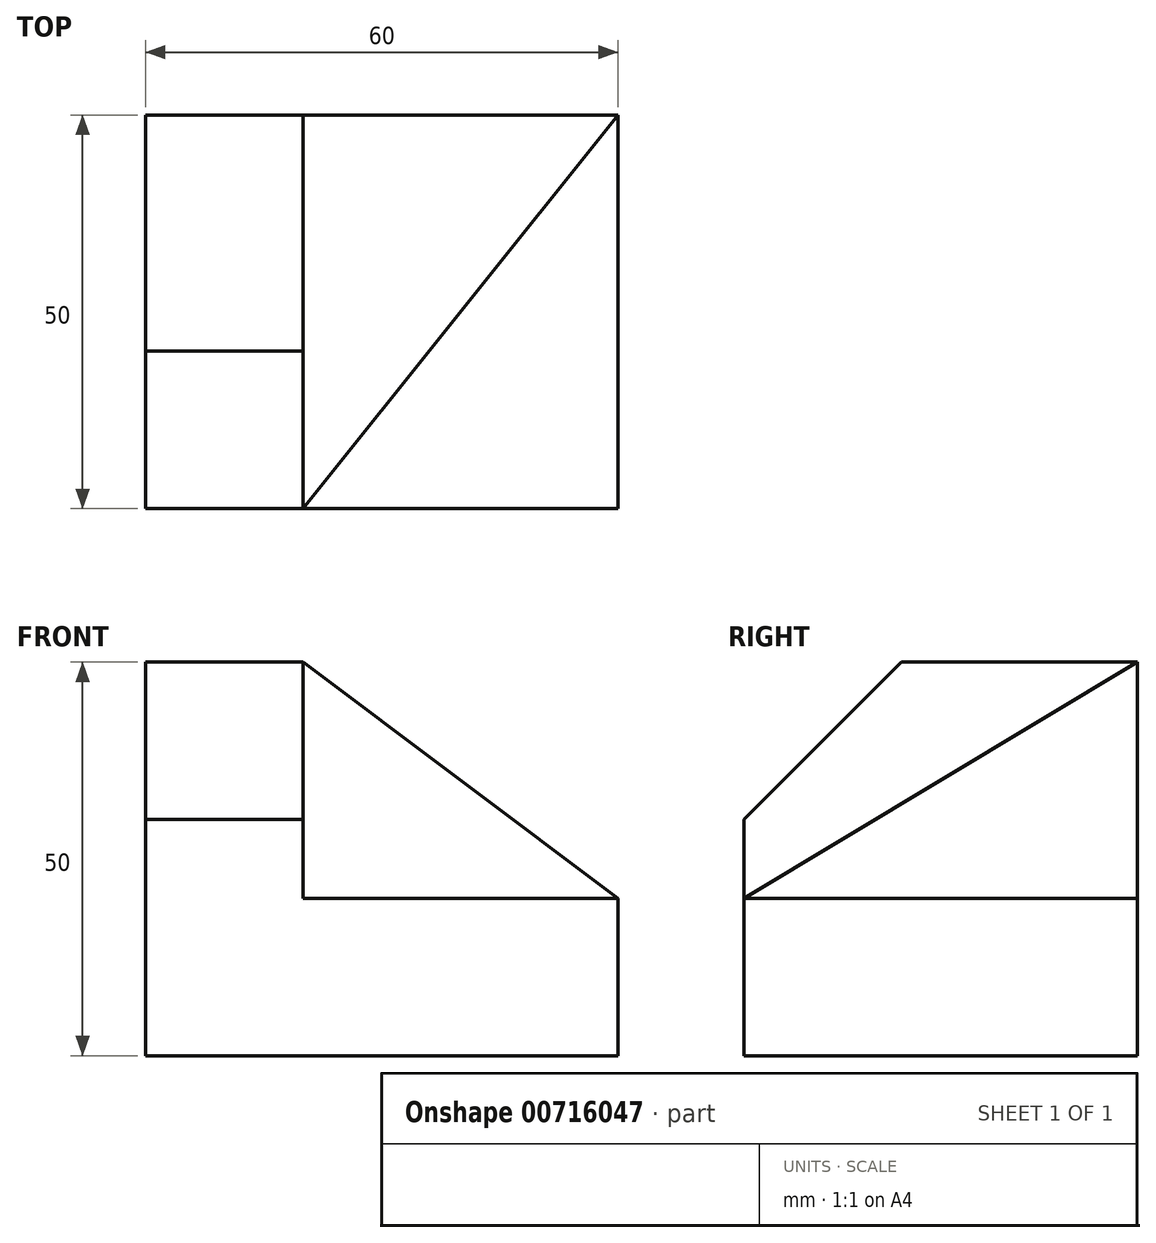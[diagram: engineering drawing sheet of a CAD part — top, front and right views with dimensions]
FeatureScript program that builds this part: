
annotation { "Feature Type Name" : "Feature", "Feature Type Description" : "" }
export const myFeature = defineFeature(function(context is Context, id is Id, definition is map)
    precondition{}
    {
        {
            var Q0;
            Q0=qCreatedBy(makeId("Top.planeOp"),FACE);
            var sketch = newSketch(context, id + "F0", { "sketchPlane" : qUnion([Q0])});
            skLineSegment(sketch, "E0.bottom", {"start": v(0, 0) * mm, "end": v(60, 0) * mm});
            skLineSegment(sketch, "E0.top", {"start": v(0, 50) * mm, "end": v(60, 50) * mm});
            skLineSegment(sketch, "E0.left", {"start": v(0, 0) * mm, "end": v(0, 50) * mm});
            skLineSegment(sketch, "E0.right", {"start": v(60, 0) * mm, "end": v(60, 50) * mm});
            skSolve(sketch);
        }
        {
            var Q0;
            Q0=makeQuery(id+"F0.imprint","IMPRINT",FACE,{"disambiguationData":[TD([[makeQuery(id+"F0.imprint","IMPRINT",EDGE,{"derivedFrom":sQuery(id+"F0.wireOp",EDGE,"E0.bottom")}),1.0]])]});
            extrude(context, id + "F1", {"entities" : qUnion([Q0]), "depth" : 50 * mm, "offsetDistance" : 25 * mm});
        }
        {
            var Q0;
            Q0=makeQuery(id+"F1.opExtrude","SWEPT_FACE",FACE,{"disambiguationData":[OSD([sQuery(id+"F0.wireOp",EDGE,"E0.bottom")])]});
            var sketch = newSketch(context, id + "F2", { "sketchPlane" : qUnion([Q0])});
            skLineSegment(sketch, "E1.bottom", {"start": v(60, 50) * mm, "end": v(20, 50) * mm});
            skLineSegment(sketch, "E1.top", {"start": v(60, 20) * mm, "end": v(20, 20) * mm});
            skLineSegment(sketch, "E1.left", {"start": v(60, 50) * mm, "end": v(60, 20) * mm});
            skLineSegment(sketch, "E1.right", {"start": v(20, 50) * mm, "end": v(20, 20) * mm});
            skSolve(sketch);
        }
        {
            var Q0;
            Q0=makeQuery(id+"F1.opExtrude","CAP_FACE",FACE,{"disambiguationData":[OSD([sQuery(id+"F0.wireOp",EDGE,"E0.bottom"),sQuery(id+"F0.wireOp",EDGE,"E0.top"),sQuery(id+"F0.wireOp",EDGE,"E0.left"),sQuery(id+"F0.wireOp",EDGE,"E0.right")])],"isStart":false});
            var sketch = newSketch(context, id + "F3", { "sketchPlane" : qUnion([Q0])});
            skLineSegment(sketch, "E2.bottom", {"start": v(0, 50) * mm, "end": v(20, 50) * mm});
            skLineSegment(sketch, "E2.top", {"start": v(0, 0) * mm, "end": v(20, 0) * mm});
            skLineSegment(sketch, "E2.left", {"start": v(0, 50) * mm, "end": v(0, 0) * mm});
            skLineSegment(sketch, "E2.right", {"start": v(20, 50) * mm, "end": v(20, 0) * mm});
            skSolve(sketch);
        }
        {
            var Q0;
            Q0=makeQuery(id+"F1.opExtrude","SWEPT_FACE",FACE,{"disambiguationData":[OSD([sQuery(id+"F0.wireOp",EDGE,"E0.right")])]});
            var sketch = newSketch(context, id + "F4", { "sketchPlane" : qUnion([Q0])});
            skLineSegment(sketch, "E3.bottom", {"start": v(0, 50) * mm, "end": v(50, 50) * mm});
            skLineSegment(sketch, "E3.top", {"start": v(0, 20) * mm, "end": v(50, 20) * mm});
            skLineSegment(sketch, "E3.left", {"start": v(0, 50) * mm, "end": v(0, 20) * mm});
            skLineSegment(sketch, "E3.right", {"start": v(50, 50) * mm, "end": v(50, 20) * mm});
            skSolve(sketch);
        }
        {
            var Q0;
            Q0=sQuery(id+"F4.wireOp",VERTEX,"E3.top.end");
            var Q1;
            Q1=sQuery(id+"F2.wireOp",VERTEX,"E1.top.end");
            var Q2;
            Q2=sQuery(id+"F3.wireOp",VERTEX,"E2.right.start");
            cPlane(context, id + "F5", {"entities" : qUnion([Q0, Q1, Q2]), "cplaneType" : CPlaneType.THREE_POINT, "offset" : 25 * mm, "width" : 150 * mm, "height" : 150 * mm});
        }
        {
            var Q0;
            Q0=makeQuery(id+"F2.imprint","IMPRINT",FACE,{"disambiguationData":[TD([[makeQuery(id+"F2.imprint","IMPRINT",EDGE,{"derivedFrom":sQuery(id+"F2.wireOp",EDGE,"E1.bottom")}),-1.0]])]});
            var Q1;
            Q1=qCreatedBy(id+"F5.planeOp",FACE);
            extrude(context, id + "F6", {"entities" : qUnion([Q0]), "operationType" : NewBodyOperationType.REMOVE, "endBound" : BoundingType.UP_TO_SURFACE, "oppositeDirection" : true, "depth" : 25 * mm, "endBoundEntityFace" : qUnion([Q1]), "offsetDistance" : 25 * mm});
        }
        {
            var Q0;
            Q0=makeQuery(id+"F1.opExtrude","CAP_EDGE",EDGE,{"disambiguationData":[OSD([sQuery(id+"F0.wireOp",EDGE,"E0.bottom")])],"isStart":false});
            chamfer(context, id + "F7", {"entities" : qUnion([Q0]), "width" : 20 * mm, "tangentPropagation" : true});
        }
    });
